# Revit family: PRD_AR_Shlvs_SaturnShelf_BXSV6-30
name_source: partatom
category: Furniture
revit_build: Autodesk Revit 2018 (Build: 20190510_1515(x64)
units: mm (PartAtom-declared; Revit-internal decimal feet)

## family parameters
Cut with Voids When Loaded = No
Host = Face
OmniClass Number = 23.40.20.00
OmniClass Title = General Furniture and Specialties
Room Calculation Point = No
Shared = No

## types (6) — shared parameters
AssetType = Fixed
Category = Pr_40_30_78_06, Bathroom shelves
Color = Stainless steel
Default Elevation = 1100 mm
DurationUnit = year
Finish = Satin finished
FinishAndColour = Stainless steel, satin finished
Form = Wall mounted
IfcExportAs = IfcFurnitureType
IfcExportType = NOTDEFINED
IntegralAccessories = Brackets welded into shelf
MainColor = stainless steel
Manufacturer = KWC Group AG
ManufacturerName = KWC Group AG
ManufacturerURL = www.kwc.com
Material = Stainless steel
NBSDescription = Shelves
NBSReference = 45-35-72/354
NominalDepth = 142 mm  [stored 0.465879 ft]
NominalHeight = 138 mm  [stored 0.452756 ft]
ProductInformation = https://pim.kwc.com
Shape = Rectangular
ShelfMaterial = PRD_AR_StainlessSteel_SatinFinished
Style = Shelve
URL = www.kwc.com
Uniclass2015Code = Pr_40_30_78_06
Uniclass2015Title = Bathroom shelves
Version = 1
WarrantyDurationUnit = year

## per-type parameters (varying)
| type | AdditionalBracket | BIMObjectName | Description | Features | GrossWeight | Model | ModelNumber | ModelReference | Name | NetWeight | NominalWidth | OverallWidth | Size | Uniclass2015Version |
| BXSV6, Width=600 | No | PRD_AR_Shelves_SaturnShelf_BXSV6 | Shelf for wall mounting, stainless steel, surface satin finished, material thickness 1 mm, brackets welded into shelf, side ends with grey plastic cover, for lengths over 1800 mm an additional bracket is scope of delivery. width: 600 mm | stainless steel, 1.00 mm, satin finished, wall mounting, 600x138x142 mm (WxHxD) | 2.20 kg | BXSV6 | 2000056952 | BXSV6 | SATURN shelf BXSV6 | 1.70 kg | 600 mm  [stored 1.9685 ft] | 600 mm  [stored 1.9685 ft] | 600 x 138 x 142 mm | Products v1.10 |
| BXSV12, Width=1200 | No | PRD_AR_Shelves_SaturnShelf_BXSV12 | Shelf for wall mounting, stainless steel, surface satin finished, material thickness 1 mm, brackets welded into shelf, side ends with grey plastic cover, for lengths over 1800 mm an additional bracket is scope of delivery. width: 1200 mm | stainless steel, 1.00 mm, satin finished, wall mounting, 1200x138x142 mm (WxHxD) | 3.50 kg | BXSV12 | 2000056946 | BXSV12 | SATURN shelf BXSV12 | 2.70 kg | 1200 mm | 1200 mm | 1200 x 138 x 142 mm | Products v1.10 |
| BXSV18, Width=1800 | Yes | PRD_AR_Shelves_SaturnShelf_BXSV18 | Shelf for wall mounting, stainless steel, surface satin finished, material thickness 1 mm, brackets welded into shelf, side ends with grey plastic cover, for lengths over 1800 mm an additional bracket is scope of delivery. width: 1800 mm | stainless steel, 1.00 mm, satin finished, wall mounting, 1800x138x142 mm (WxHxD) | 4.90 kg | BXSV18 | 2000056950 | BXSV18 | SATURN shelf BXSV18 | 3.80 kg | 1800 mm  [stored 5.90551 ft] | 1800 mm  [stored 5.90551 ft] | 1800 x 138 x 142 mm | Products v1.5 |
| BXSV24, Width=2400 | Yes | PRD_AR_Shelves_SaturnShelf_BXSV24 | Shelf for wall mounting, stainless steel, surface satin finished, material thickness 1 mm, brackets welded into shelf, side ends with grey plastic cover, for lengths over 1800 mm an additional bracket is scope of delivery. width: 2400 mm | stainless steel, 1.00 mm, satin finished, wall mounting, 2400x138x142 mm (WxHxD) | 6.00 kg | BXSV24 | 2000100088 | BXSV24 | SATURN shelf BXSV24 | 4.60 kg | 2400 mm | 2400 mm | 2400 x 138 x 142 mm | Products v1.10 |
| BXSV16, Width=1600 | No | PRD_AR_Shelves_SaturnShelf_BXSV16 | Shelf for wall mounting, stainless steel, surface satin finished, material thickness 1 mm, brackets welded into shelf, side ends with grey plastic cover, for lengths over 1800 mm an additional bracket is scope of delivery. width: 1600 mm | stainless steel, 1.00 mm, satin finished, wall mounting, 1600x138x142 mm (WxHxD) | 3.80 kg | BXSV16 | 2030046197 | BXSV16 | SATURN shelf BXSV16 | 2.90 kg | 1600 mm  [stored 5.24934 ft] | 1600 mm  [stored 5.24934 ft] | 1600 x 138 x 142 mm | Products v1.10 |
| BXSV30, Width=3000 | Yes | PRD_AR_Shelves_SaturnShelf_BXSV30 | Shelf for wall mounting, stainless steel, surface satin finished, material thickness 1 mm, brackets welded into shelf, side ends with grey plastic cover, for lengths over 1800 mm an additional bracket is scope of delivery. width: 3000 mm | stainless steel, 1.00 mm, satin finished, wall mounting, 3000x138x142 mm (WxHxD) | 6.60 kg | BXSV30 | 2030046195 | BXSV30 | SATURN shelf BXSV30 | 4.80 kg | 3000 mm  [stored 9.84252 ft] | 3000 mm  [stored 9.84252 ft] | 3000 x 138 x 142 mm | Products v1.10 |

note: [stored X ft] marks values corroborated as IEEE doubles in the binary element streams (Revit-internal decimal feet)

## geometry (parser evidence)
native form markers: Sweep x2
no freeform markers — native parametric forms only
